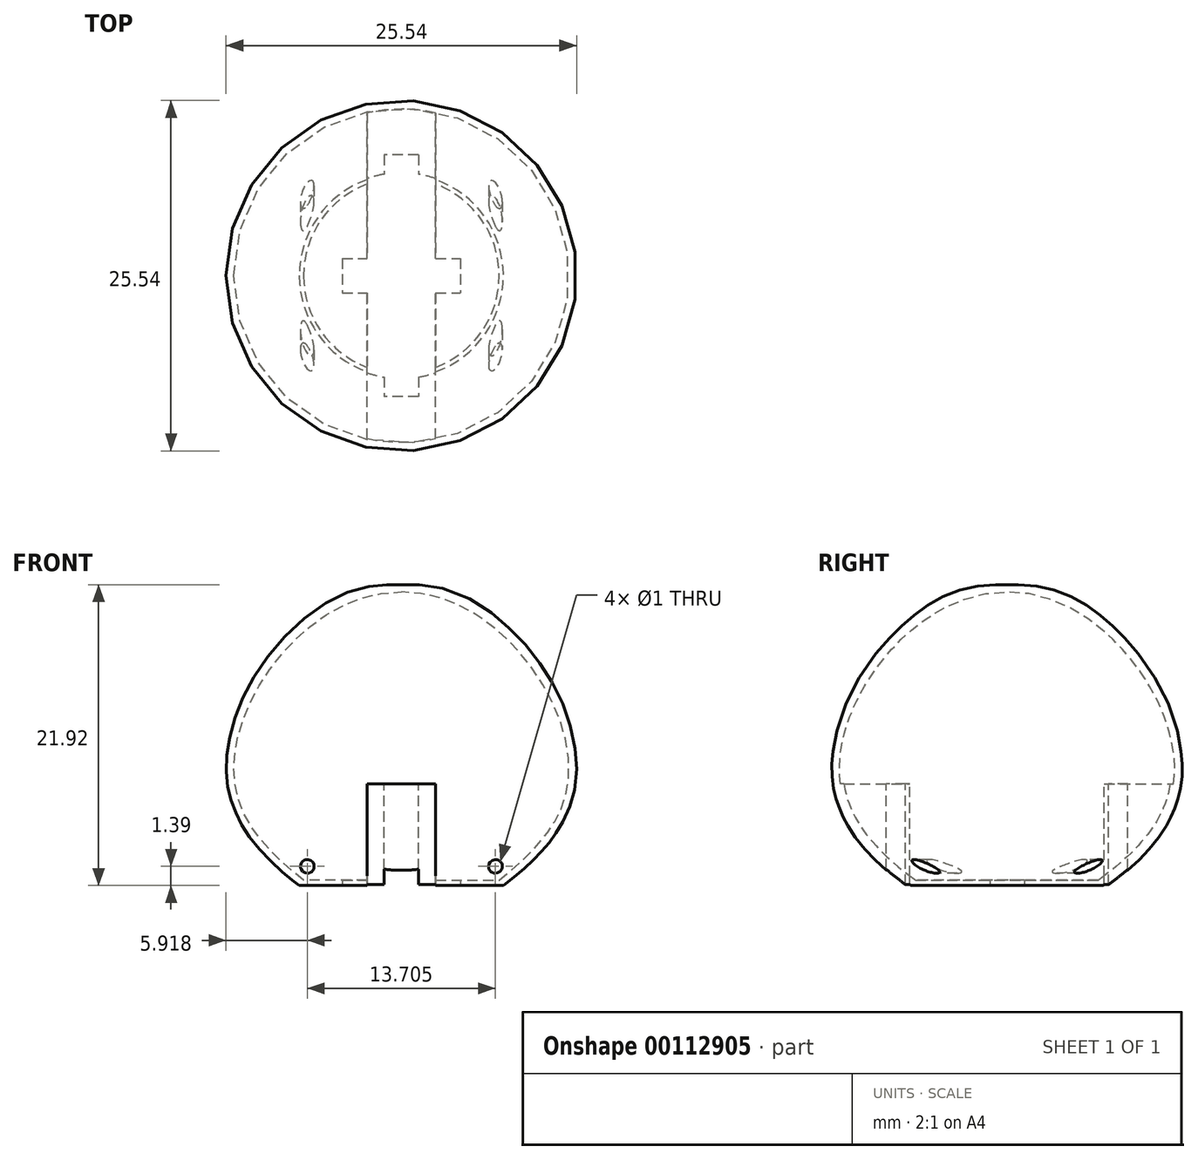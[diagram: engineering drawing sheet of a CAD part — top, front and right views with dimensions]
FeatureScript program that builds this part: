
annotation { "Feature Type Name" : "Feature", "Feature Type Description" : "" }
export const myFeature = defineFeature(function(context is Context, id is Id, definition is map)
    precondition{}
    {
        {
            var Q0;
            Q0=qCreatedBy(makeId("Front.planeOp"),FACE);
            var sketch = newSketch(context, id + "F0", { "sketchPlane" : qUnion([Q0])});
            skLineSegment(sketch, "E0", {"start": v(0, 1) * mm, "end": v(-7.13, 1) * mm});
            skFitSpline(sketch, "E1", {"points": [v(-7.13, 1) * mm, v(-11.8, 6.63) * mm, v(-10.15, 15.5) * mm, v(0, 22) * mm], "startDerivative": vector(-16.7, 12.87) * mm, "endDerivative": vector(34.43, 0) * mm});
            skFitSpline(sketch, "E2.0", {"points": [v(-7.43, 0.61) * mm, v(-7.78, 0.88) * mm, v(-8.54, 1.5) * mm, v(-9.73, 2.59) * mm, v(-10.86, 3.86) * mm, v(-11.66, 5.06) * mm, v(-12.15, 6.1) * mm, v(-12.53, 7.21) * mm, v(-12.75, 8.65) * mm, v(-12.67, 10.45) * mm, v(-12.12, 12.88) * mm, v(-10.68, 15.9) * mm, v(-7.96, 19.27) * mm, v(-4.38, 21.8) * mm, v(-1.51, 22.5) * mm, v(0, 22.5) * mm]});
            skLineSegment(sketch, "E3", {"start": v(-7.43, 0.61) * mm, "end": v(0, 0.61) * mm});
            skLineSegment(sketch, "E4", {"start": v(0, 0.61) * mm, "end": v(0, 1) * mm});
            skLineSegment(sketch, "E5", {"start": v(0, 22.5) * mm, "end": v(0, 22) * mm});
            skSolve(sketch);
        }
        {
            var Q0;
            Q0 = qSketchRegion(id + "F0", true);
            var Q1;
            Q1=sQuery(id+"F0.wireOp",EDGE,"E5");
            revolve(context, id + "F1", {"entities" : qUnion([Q0]), "axis" : qUnion([Q1]), "revolveType" : RevolveType.FULL});
        }
        {
            var Q0;
            Q0=qCreatedBy(makeId("Front.planeOp"),FACE);
            var sketch = newSketch(context, id + "F2", { "sketchPlane" : qUnion([Q0])});
            skLineSegment(sketch, "E6.bottom", {"start": v(2.5, 0) * mm, "end": v(-2.5, 0) * mm});
            skLineSegment(sketch, "E6.top", {"start": v(2.5, 8) * mm, "end": v(-2.5, 8) * mm});
            skLineSegment(sketch, "E6.left", {"start": v(2.5, 0) * mm, "end": v(2.5, 8) * mm});
            skLineSegment(sketch, "E6.right", {"start": v(-2.5, 0) * mm, "end": v(-2.5, 8) * mm});
            skPoint(sketch, "E6.middle", {"position": v(0, 4) * mm});
            skSolve(sketch);
        }
        {
            var Q0;
            Q0=qSketchRegion(id+"F2",true);
            extrude(context, id + "F3", {"entities" : qUnion([Q0]), "endBound" : BoundingType.UP_TO_NEXT, "depth" : 25 * mm});
        }
        {
            var Q0;
            Q0=makeQuery(id+"F3.opExtrude","CAP_FACE",FACE,{"disambiguationData":[OSD([sQuery(id+"F2.wireOp",EDGE,"E6.bottom"),sQuery(id+"F2.wireOp",EDGE,"E6.top"),sQuery(id+"F2.wireOp",EDGE,"E6.left"),sQuery(id+"F2.wireOp",EDGE,"E6.right")])],"isStart":true});
            extrude(context, id + "F4", {"entities" : qUnion([Q0]), "operationType" : NewBodyOperationType.ADD, "endBound" : BoundingType.UP_TO_NEXT, "depth" : 25 * mm});
        }
        {
            var Q0;
            {var subQ0=sQuery(id+"F2.wireOp",EDGE,"E6.top");Q0=makeQuery(id+"F4.boolean.opBoolean","MERGE",FACE,{"derivedFrom":[makeQuery(id+"F3.opExtrude","SWEPT_FACE",FACE,{"disambiguationData":[OSD([subQ0])]}),makeQuery(id+"F4.opExtrude","SWEPT_FACE",FACE,{"disambiguationData":[OSD([subQ0])]})]});}
            var sketch = newSketch(context, id + "F5", { "sketchPlane" : qUnion([Q0])});
            skLineSegment(sketch, "E7.bottom", {"start": v(1.25, 8.8) * mm, "end": v(-1.25, 8.8) * mm});
            skLineSegment(sketch, "E7.top", {"start": v(1.25, -8.8) * mm, "end": v(-1.25, -8.8) * mm});
            skLineSegment(sketch, "E7.left", {"start": v(1.25, 8.8) * mm, "end": v(1.25, 7.4) * mm});
            skLineSegment(sketch, "E7.right", {"start": v(-1.25, 8.8) * mm, "end": v(-1.25, 7.4) * mm});
            skPoint(sketch, "E7.middle", {"position": v(0, 0) * mm});
            skArc(sketch, "E8", {"start": v(-1.25, 7.4) * mm, "mid": v(-1.88, 7.26) * mm, "end": v(-2.5, 7.07) * mm});
            skLineSegment(sketch, "E9.trimOffspring", {"start": v(-1.25, -7.4) * mm, "end": v(-1.25, -8.8) * mm});
            skLineSegment(sketch, "E10.trimOffspring", {"start": v(1.25, -7.4) * mm, "end": v(1.25, -8.8) * mm});
            skArc(sketch, "E11.trimOffspring", {"start": v(1.25, -7.4) * mm, "mid": v(1.88, -7.26) * mm, "end": v(2.5, -7.07) * mm});
            skLineSegment(sketch, "E12", {"start": v(-2.5, 7.07) * mm, "end": v(-2.5, -7.07) * mm});
            skLineSegment(sketch, "E13", {"start": v(2.5, 7.07) * mm, "end": v(2.5, -7.07) * mm});
            skArc(sketch, "E14.trimOffspring", {"start": v(-2.5, -7.07) * mm, "mid": v(-1.88, -7.26) * mm, "end": v(-1.25, -7.4) * mm});
            skArc(sketch, "E15.trimOffspring", {"start": v(2.5, 7.07) * mm, "mid": v(1.88, 7.26) * mm, "end": v(1.25, 7.4) * mm});
            skSolve(sketch);
        }
        {
            var Q0;
            Q0=qSketchRegion(id+"F5",true);
            extrude(context, id + "F6", {"entities" : qUnion([Q0]), "operationType" : NewBodyOperationType.REMOVE, "oppositeDirection" : true, "depth" : 25 * mm});
        }
        {
            var Q0;
            Q0=makeQuery(id+"F1.opRevolve","SWEPT_FACE",FACE,{"disambiguationData":[OSD([sQuery(id+"F0.wireOp",EDGE,"E3")])]});
            var sketch = newSketch(context, id + "F7", { "sketchPlane" : qUnion([Q0])});
            skLineSegment(sketch, "E16.bottom", {"start": v(4.3, 1.25) * mm, "end": v(-4.3, 1.25) * mm});
            skLineSegment(sketch, "E16.top", {"start": v(4.3, -1.25) * mm, "end": v(-4.3, -1.25) * mm});
            skLineSegment(sketch, "E16.left", {"start": v(4.3, 1.25) * mm, "end": v(4.3, -1.25) * mm});
            skLineSegment(sketch, "E16.right", {"start": v(-4.3, 1.25) * mm, "end": v(-4.3, -1.25) * mm});
            skPoint(sketch, "E16.middle", {"position": v(0, 0) * mm});
            skSolve(sketch);
        }
        {
            var Q0;
            Q0=qSketchRegion(id+"F7",true);
            extrude(context, id + "F8", {"entities" : qUnion([Q0]), "operationType" : NewBodyOperationType.REMOVE, "endBound" : BoundingType.SYMMETRIC, "oppositeDirection" : true, "depth" : 3 * mm});
        }
        {
            var Q0;
            Q0=qCreatedBy(makeId("Front.planeOp"),FACE);
            var sketch = newSketch(context, id + "F9", { "sketchPlane" : qUnion([Q0])});
            skCircle(sketch, "E17", {"center": v(-6.85, 2) * mm, "radius": 0.5 * mm});
            skCircle(sketch, "E18.MirrorC", {"center": v(6.85, 2) * mm, "radius": 0.5 * mm});
            skSolve(sketch);
        }
        {
            var Q0;
            Q0=qSketchRegion(id+"F9",true);
            extrude(context, id + "F10", {"entities" : qUnion([Q0]), "operationType" : NewBodyOperationType.REMOVE, "endBound" : BoundingType.SYMMETRIC, "oppositeDirection" : true, "depth" : 25 * mm});
        }
        {
            var Q0;
            Q0=qCreatedBy(makeId("Top.planeOp"),FACE);
            var sketch = newSketch(context, id + "F11", { "sketchPlane" : qUnion([Q0])});
            skLineSegment(sketch, "E19.bottom", {"start": v(4, 1) * mm, "end": v(-4, 1) * mm});
            skLineSegment(sketch, "E19.top", {"start": v(4, -1) * mm, "end": v(-4, -1) * mm});
            skLineSegment(sketch, "E19.left", {"start": v(4, 1) * mm, "end": v(4, -1) * mm});
            skLineSegment(sketch, "E19.right", {"start": v(-4, 1) * mm, "end": v(-4, -1) * mm});
            skPoint(sketch, "E19.middle", {"position": v(0, 0) * mm});
            skSolve(sketch);
        }
        {
            var Q0;
            Q0 = qSketchRegion(id + "F11", true);
            extrude(context, id + "F12", {"entities" : qUnion([Q0]), "operationType" : NewBodyOperationType.REMOVE, "oppositeDirection" : true, "depth" : 20 * mm});
        }
    });
